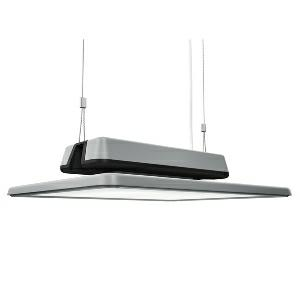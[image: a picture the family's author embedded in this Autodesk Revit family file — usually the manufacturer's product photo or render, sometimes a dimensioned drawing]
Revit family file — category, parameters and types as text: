
# Revit family: acaneo_-_hial_20000_850_n_ea_00734314_38f4
name_source: partatom
category: Lighting Fixtures
units: mm (PartAtom-declared; Revit-internal decimal feet)

## family parameters
Cut with Voids When Loaded = No
Host = Face
Light Source = No
Part Type = Normal
Room Calculation Point = No
Round Connector Dimension = Use Diameter
Shared = No

## types (1)
- ACANEO - HIAL 20000/850/N/EA (1 x LED, 22000 lm, 5000K)
    Apparent Load = 140 VA
    Approval mark = CE
    CIE Flux Codes = 84 97 100 100 100
    Color Rendering = 80-89
    Color Temperature = 5000K
    Control Gear = Electronic ballast
    Default Elevation = 1800 mm
    Description = HIAL 20000/850/N/EA|High bay luminaire|light source: LED|work equipment: Electronic ballast|connected load: 220-240 V, 50/60 Hz|Power consumption: approx. 140 W|power factor: approx. 0,951|luminous flux: 22000 lm|luminous efficacy: 157 lm/W|colour temperature: Cold white, ca. 5000 K|color rendering index (CRI): >= 80|chromaticity tolerance:  3 SDCM|System of protection: IP 65|class of protection: I|technology: Switchable|luminaire body|material: Aluminium|surface: Powder coatet|colour: White aluminium|lamp cover: Acrylic (PMMA), Clear|weight (net): approx. 8.2 kg|mains lead: Built-in plug RST 25i3 Einbau|Fastening: Available separately|Accessory: Junction box (RST 2013)|minimum ambient temperature: -30 ░C|maximum ambient temperature: 50 ░C|glare control: Optics|unified glare rating(4H 8H): <=  22|
    Frequency = 50 Hz, 60 Hz
    Height = 125 mm
    Lamp = 1 x LED
    Lamp Light Flux = 22000 lm
    Lamp count = 1
    Length = 480 mm
    Luminous efficacy = 157 lm/W
    Manufacturer = Waldmann
    ModVariant = No
    Model = 00734314
    Mounting Place = Ceiling
    Mounting Type = Pendant
    Number of Poles = 1
    OnlyDefault = Yes
    Power Factor = 1
    Product Name = ACANEO - HIAL 20000/850/N/EA
    Product group = High bay luminaire (industry)
    ProductGroupID = 901
    Protection Class = Protection class I
    Protection Degree = IP 65
    RLX_Detail_Level = 1
    RLX_Emergency_Light_Flux = 0 lm
    RLX_Emergency_Type = 0
    RLX_Emergency_Type_DB = No
    RlxData = <blob elided: 30277 chars, md5=d759697f>
    Socket = socket
    Standby Power = 0 W
    System Light Flux = 22000 lm
    System Power = 140 W
    Type Comments = Product without accessories
    Type Image = acaneo-hial.jpg
    URL = http://relux.com
    VarID = ---
    Voltage = 230 V
    Voltage Range = 110-120 V, 220-240 V
    Weight = 0.00 kg
    Width = 405 mm

## geometry (parser evidence)
native form markers: Blend x4, Sweep x9
no freeform markers — native parametric forms only
